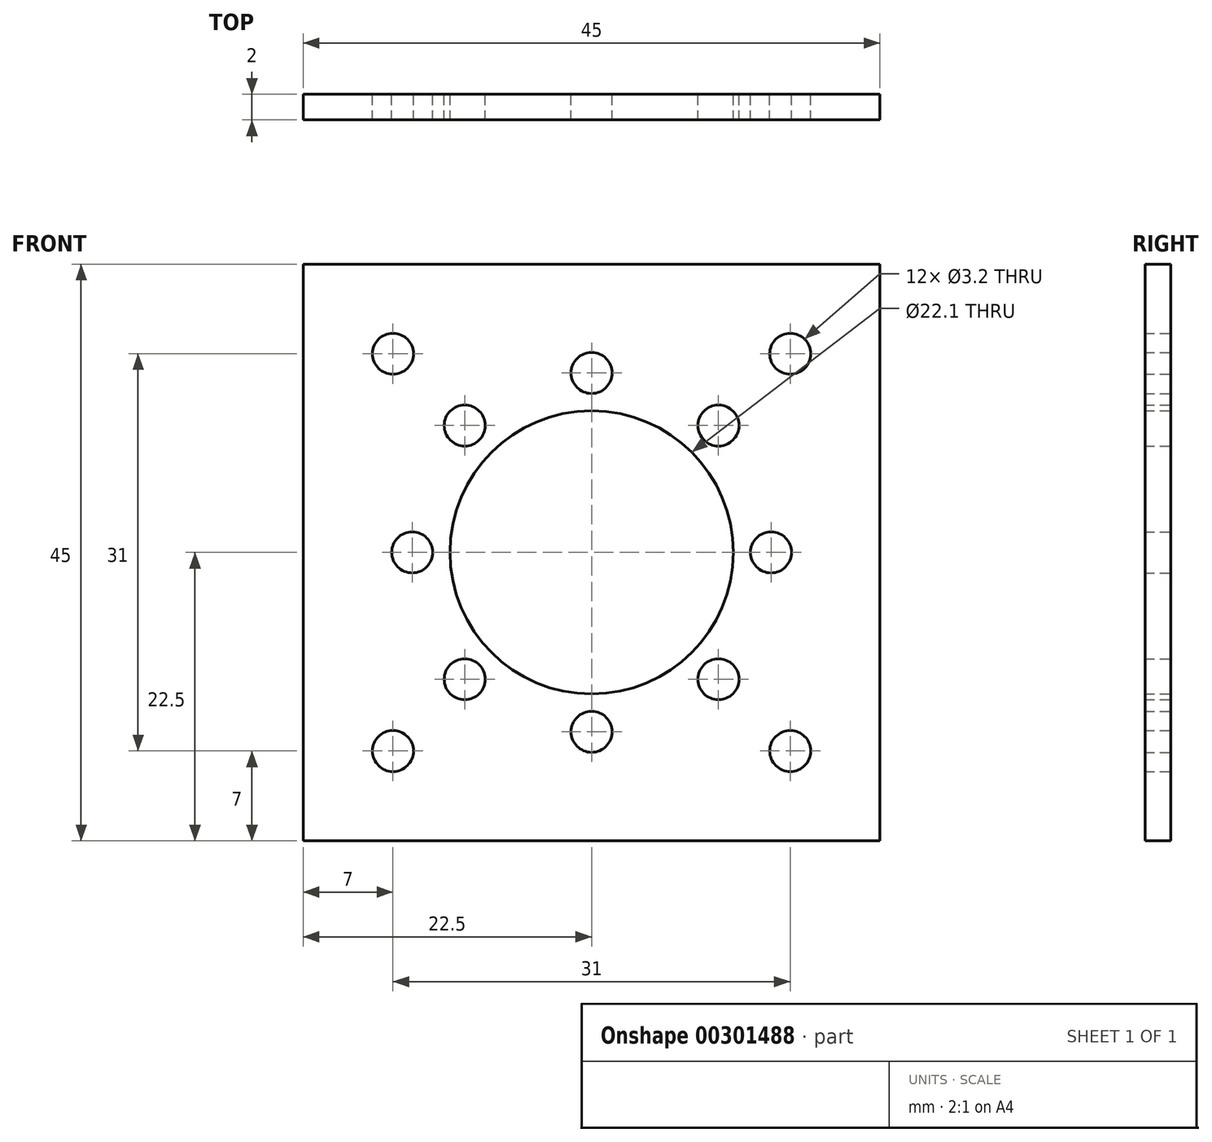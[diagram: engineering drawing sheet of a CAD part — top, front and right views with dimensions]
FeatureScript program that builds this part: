
annotation { "Feature Type Name" : "Feature", "Feature Type Description" : "" }
export const myFeature = defineFeature(function(context is Context, id is Id, definition is map)
    precondition{}
    {
        {
            var Q0;
            Q0=qCreatedBy(makeId("Front.planeOp"),FACE);
            var sketch = newSketch(context, id + "F0", { "sketchPlane" : qUnion([Q0])});
            skLineSegment(sketch, "E0.bottom", {"start": v(22.5, -22.5) * mm, "end": v(-22.5, -22.5) * mm});
            skLineSegment(sketch, "E0.top", {"start": v(22.5, 22.5) * mm, "end": v(-22.5, 22.5) * mm});
            skLineSegment(sketch, "E0.left", {"start": v(22.5, -22.5) * mm, "end": v(22.5, 22.5) * mm});
            skLineSegment(sketch, "E0.right", {"start": v(-22.5, -22.5) * mm, "end": v(-22.5, 22.5) * mm});
            skPoint(sketch, "E0.middle", {"position": v(0, 0) * mm});
            skCircle(sketch, "E1", {"center": v(0, 0) * mm, "radius": 11.05 * mm});
            skCircle(sketch, "E2", {"center": v(0, 0) * mm, "radius": 14 * mm});
            skPoint(sketch, "E3", {"position": v(-14, 0) * mm});
            skCircle(sketch, "E4", {"center": v(-14, 0) * mm, "radius": 1.6 * mm});
            skCircle(sketch, "E5.1.0", {"center": v(-9.9, -9.9) * mm, "radius": 1.6 * mm});
            skCircle(sketch, "E5.2.0", {"center": v(0, -14) * mm, "radius": 1.6 * mm});
            skCircle(sketch, "E5.3.0", {"center": v(9.9, -9.9) * mm, "radius": 1.6 * mm});
            skCircle(sketch, "E5.4.0", {"center": v(14, 0) * mm, "radius": 1.6 * mm});
            skCircle(sketch, "E5.5.0", {"center": v(9.9, 9.9) * mm, "radius": 1.6 * mm});
            skCircle(sketch, "E5.6.0", {"center": v(0, 14) * mm, "radius": 1.6 * mm});
            skCircle(sketch, "E5.7.0", {"center": v(-9.9, 9.9) * mm, "radius": 1.6 * mm});
            skCircle(sketch, "E6", {"center": v(-15.5, 15.5) * mm, "radius": 1.6 * mm});
            skCircle(sketch, "E7", {"center": v(-15.5, -15.5) * mm, "radius": 1.6 * mm});
            skCircle(sketch, "E8.MirrorC", {"center": v(15.5, 15.5) * mm, "radius": 1.6 * mm});
            skCircle(sketch, "E9.MirrorC", {"center": v(15.5, -15.5) * mm, "radius": 1.6 * mm});
            skSolve(sketch);
        }
        {
            var Q0;
            Q0=makeQuery(id+"F0.imprint","IMPRINT",FACE,{"disambiguationData":[TD([[makeQuery(id+"F0.imprint","IMPRINT",EDGE,{"derivedFrom":sQuery(id+"F0.wireOp",EDGE,"E0.bottom")}),-1.0]])]});
            var Q1;
            Q1=makeQuery(id+"F0.imprint","IMPRINT",FACE,{"disambiguationData":[TD([[makeQuery(id+"F0.imprint","IMPRINT",EDGE,{"derivedFrom":sQuery(id+"F0.wireOp",EDGE,"E1")}),-1.0]])]});
            extrude(context, id + "F1", {"entities" : qUnion([Q0, Q1]), "depth" : 2 * mm});
        }
    });
